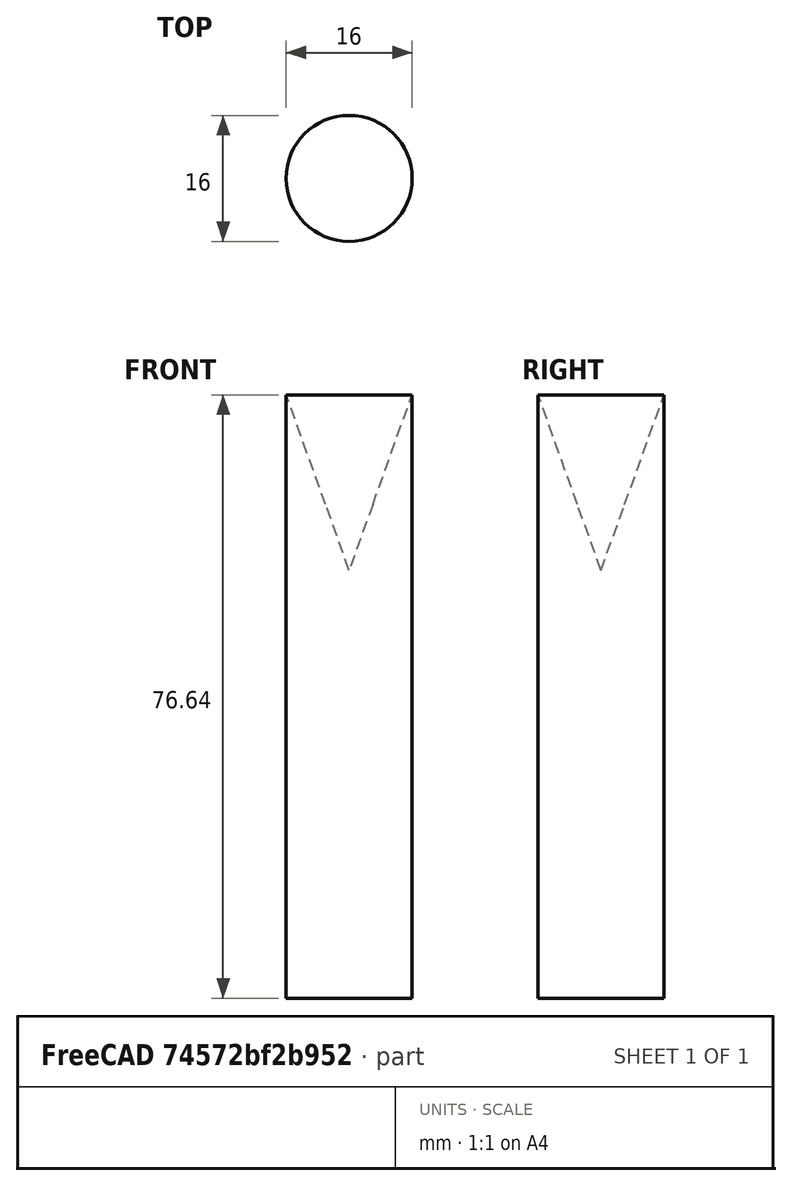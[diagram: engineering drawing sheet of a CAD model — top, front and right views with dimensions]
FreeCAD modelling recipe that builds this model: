
FCSTD DOCUMENT  (FreeCAD 0.19R24291 (Git))
Label: retrograde marker
License: All rights reserved
LicenseURL: http://en.wikipedia.org/wiki/All_rights_reserved
objects: Sketcher::SketchObject×1, PartDesign::Revolution×1, PartDesign::Body×1
note: 4 computed .brp shape members not serialized (recipe doc carries the construction recipe); baked Part::Feature solids carry a one-line shape summary decoded from their .brp

FEATURE [Sketcher::SketchObject] Sketch
  FullyConstrained = false
  MapMode = 5
  Placement = pos=(0,0,0) rot=(1,0,0;1.5708rad)
  Support = -> [XZ_Plane]
  sketch-geometry (9):
    g0: LineSegment StartX=8 StartY=0 StartZ=0 EndX=0 EndY=0 EndZ=0
    g1: LineSegment StartX=0 StartY=0 StartZ=0 EndX=0 EndY=37.71 EndZ=0
    g2: LineSegment StartX=8 StartY=62.71 StartZ=0 EndX=8 EndY=0 EndZ=0
    g3: LineSegment StartX=8 StartY=62.71 StartZ=0 EndX=3 EndY=62.71 EndZ=0
    g4: LineSegment StartX=3 StartY=62.71 StartZ=0 EndX=0 EndY=54.3513 EndZ=0
    g5: LineSegment StartX=3 StartY=62.71 StartZ=0 EndX=8 EndY=76.6412 EndZ=0
    g6: LineSegment StartX=0 StartY=37.71 StartZ=0 EndX=0 EndY=54.3513 EndZ=0
    g7: GeomPoint X=-12.3299 Y=78.4324 Z=0
    g8: LineSegment StartX=8 StartY=62.71 StartZ=0 EndX=8 EndY=76.6412 EndZ=0
  constraints (22):
    c: Coincident(g0,g1)
    c: Vertical(g2)
    c: Coincident(g0,g2)
    c: Horizontal(g0)
    c: Vertical(g1)
    c: Coincident(g3,g2)
    c: Horizontal(g3)
    c: Coincident(g4,g3)
    c: Distance(g0) = 8
    c: Distance(g2) = 62.71
    c: Distance(g1) = 37.71
    c: Distance(g3) = 5
    c: Coincident(g5,g3)
    c: Coincident(g6,g1)
    c: Vertical(g6)
    c: Parallel(g5,g4)
    c: Coincident(g8,g2)
    c: Coincident(g5,g8)
    c: Vertical(g8)
    c: Coincident(g4,g6)
    c: Coincident(g0,g-1)
    c: DistanceY(g4,g5) = 22.29
FEATURE [PartDesign::Revolution] Revolution
  Angle = 360
  Axis = (0,-2e-16,1)
  Base = (0,0,0)
  Placement = pos=(0,0,0) rot=(1,0,0;1.5708rad)
  Profile = -> Sketch
  ReferenceAxis = -> Sketch [V_Axis]
FEATURE [PartDesign::Body] Body
  Group = -> [Sketch,Revolution]
  Origin = -> Origin
  Tip = -> Revolution
